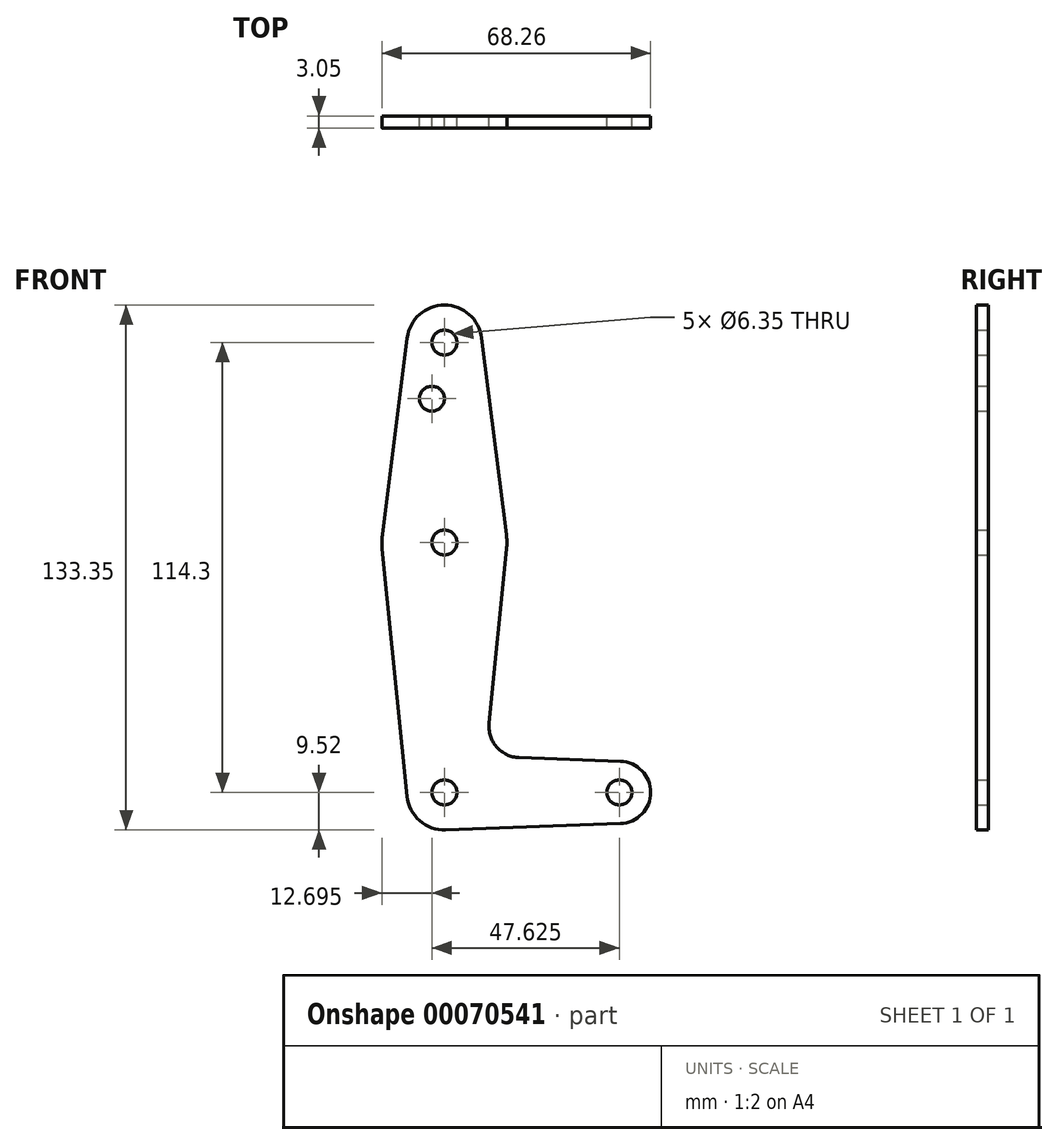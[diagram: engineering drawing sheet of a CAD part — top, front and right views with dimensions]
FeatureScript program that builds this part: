
annotation { "Feature Type Name" : "Feature", "Feature Type Description" : "" }
export const myFeature = defineFeature(function(context is Context, id is Id, definition is map)
    precondition{}
    {
        {
            var Q0;
            Q0=qCreatedBy(makeId("Front.planeOp"),FACE);
            var sketch = newSketch(context, id + "F0", { "sketchPlane" : qUnion([Q0])});
            skLineSegment(sketch, "E0", {"start": v(0, 0) * mm, "end": v(0, 114.3) * mm, "construction": true});
            skLineSegment(sketch, "E1", {"start": v(0, 0) * mm, "end": v(44.45, 0) * mm, "construction": true});
            skCircle(sketch, "E2", {"center": v(0, 0) * mm, "radius": 9.53 * mm});
            skCircle(sketch, "E3", {"center": v(0, 114.3) * mm, "radius": 9.53 * mm});
            skCircle(sketch, "E4", {"center": v(0, 63.5) * mm, "radius": 15.88 * mm});
            skCircle(sketch, "E5", {"center": v(44.45, 0) * mm, "radius": 7.94 * mm});
            skLineSegment(sketch, "E6", {"start": v(-9.45, 115.5) * mm, "end": v(-15.75, 65.48) * mm});
            skLineSegment(sketch, "E7", {"start": v(9.45, 115.5) * mm, "end": v(15.75, 65.48) * mm});
            skLineSegment(sketch, "E8", {"start": v(-15.8, 61.91) * mm, "end": v(-9.48, -0.95) * mm});
            skLineSegment(sketch, "E9", {"start": v(15.8, 61.91) * mm, "end": v(11.34, 17.6) * mm});
            skLineSegment(sketch, "E10", {"start": v(18.97, 8.85) * mm, "end": v(44.73, 7.93) * mm});
            skLineSegment(sketch, "E11", {"start": v(44.73, -7.93) * mm, "end": v(0.34, -9.52) * mm});
            skCircle(sketch, "E12", {"center": v(0, 114.3) * mm, "radius": 3.18 * mm});
            skCircle(sketch, "E13", {"center": v(0, 63.5) * mm, "radius": 3.18 * mm});
            skCircle(sketch, "E14", {"center": v(0, 0) * mm, "radius": 3.18 * mm});
            skCircle(sketch, "E15", {"center": v(44.45, 0) * mm, "radius": 3.18 * mm});
            skCircle(sketch, "E16", {"center": v(-3.17, 100.03) * mm, "radius": 3.18 * mm});
            skArc(sketch, "E17.filletArc", {"start": v(11.34, 17.6) * mm, "mid": v(13.26, 11.57) * mm, "end": v(18.97, 8.85) * mm});
            skSolve(sketch);
        }
        {
            var Q0;
            Q0 = qSketchRegion(id + "F0", true);
            extrude(context, id + "F1", {"entities" : qUnion([Q0]), "depth" : 3.05 * mm});
        }
    });
